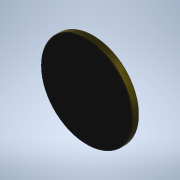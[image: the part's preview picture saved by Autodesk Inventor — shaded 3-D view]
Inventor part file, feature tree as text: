
AUTODESK INVENTOR PART (.ipt)
format: ipt  version: 2020 (Build 240168000, 168)  size: 111,616 bytes
history: native  units: mm
features: extrude x1, fillet x1, sketch x1
ambient origin geometry x8: Origin, YZ Plane, XZ Plane, XY Plane, X Axis, Y Axis, Z Axis, Center Point
bodies: Solid1 (feature_tree)
feature tree (3):
  extrude  "Extrusion1"  Depth=2.0mm TaperAngle=0.0deg
  fillet  "Fillet1"  Radius=0.5mm
  sketch  "Sketch1"  dims[d0=25.0mm d1=2.0mm d2=0.0mm d3=0.5mm]
